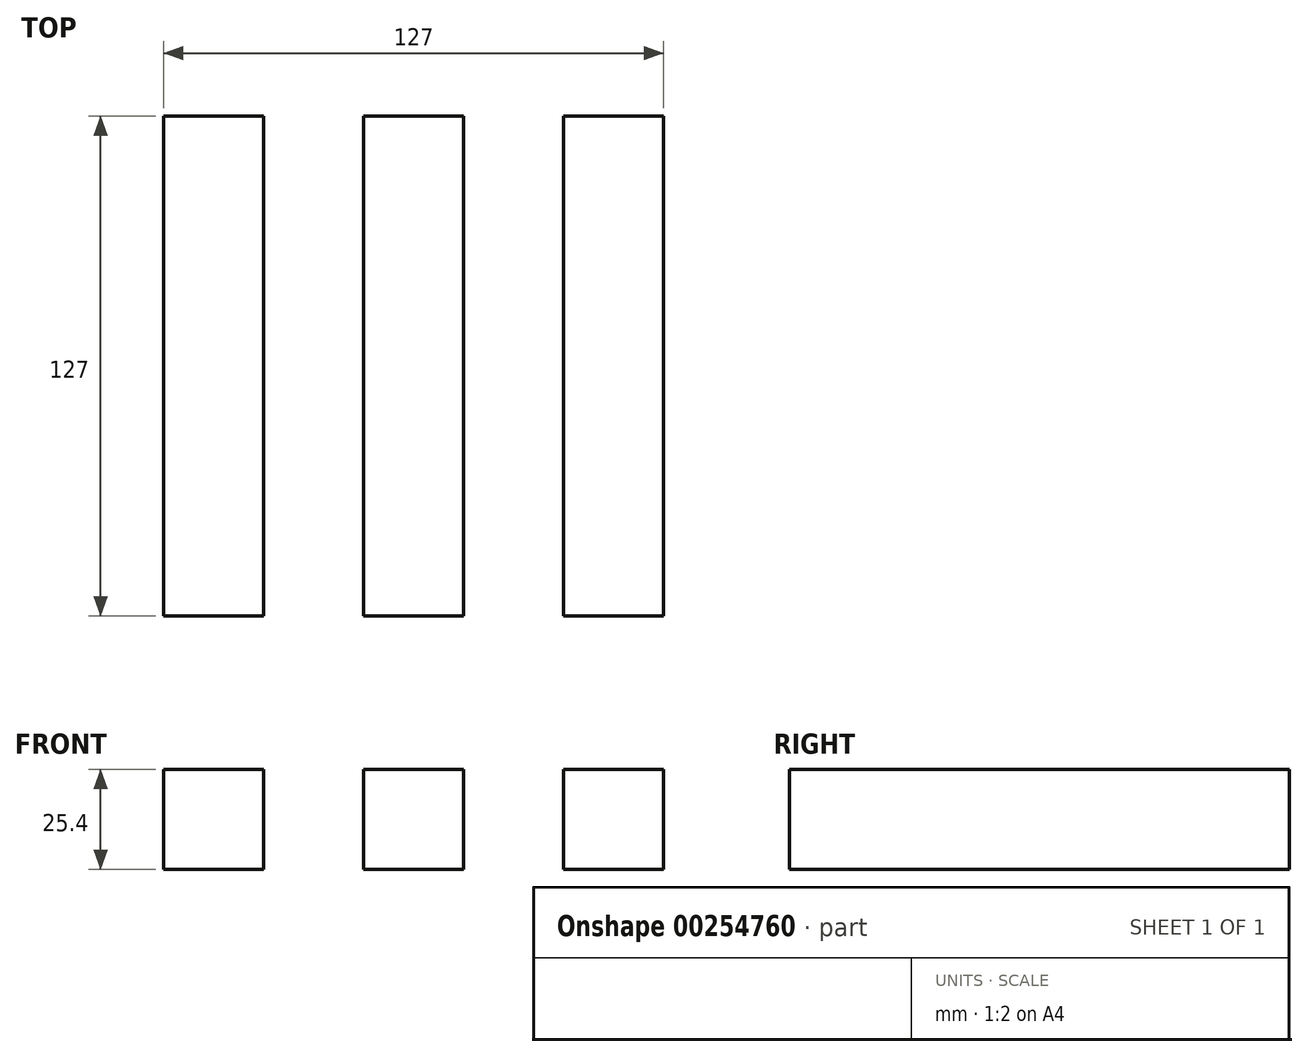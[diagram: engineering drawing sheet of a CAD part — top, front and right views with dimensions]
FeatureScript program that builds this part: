
annotation { "Feature Type Name" : "Feature", "Feature Type Description" : "" }
export const myFeature = defineFeature(function(context is Context, id is Id, definition is map)
    precondition{}
    {
        {
            var Q0;
            Q0=qCreatedBy(makeId("Front.planeOp"),FACE);
            var sketch = newSketch(context, id + "F0", { "sketchPlane" : qUnion([Q0])});
            skLineSegment(sketch, "E0.bottom", {"start": v(12.7, 12.7) * mm, "end": v(-12.7, 12.7) * mm});
            skLineSegment(sketch, "E0.top", {"start": v(12.7, -12.7) * mm, "end": v(-12.7, -12.7) * mm});
            skLineSegment(sketch, "E0.left", {"start": v(12.7, 12.7) * mm, "end": v(12.7, -12.7) * mm});
            skLineSegment(sketch, "E0.right", {"start": v(-12.7, 12.7) * mm, "end": v(-12.7, -12.7) * mm});
            skPoint(sketch, "E0.middle", {"position": v(0, 0) * mm});
            skLineSegment(sketch, "E1.bottom", {"start": v(63.5, 12.7) * mm, "end": v(38.1, 12.7) * mm});
            skLineSegment(sketch, "E1.top", {"start": v(63.5, -12.7) * mm, "end": v(38.1, -12.7) * mm});
            skLineSegment(sketch, "E1.left", {"start": v(63.5, 12.7) * mm, "end": v(63.5, -12.7) * mm});
            skLineSegment(sketch, "E1.right", {"start": v(38.1, 12.7) * mm, "end": v(38.1, -12.7) * mm});
            skPoint(sketch, "E1.middle", {"position": v(50.8, 0) * mm});
            skLineSegment(sketch, "E2.bottom", {"start": v(-38.1, 12.7) * mm, "end": v(-63.5, 12.7) * mm});
            skLineSegment(sketch, "E2.top", {"start": v(-38.1, -12.7) * mm, "end": v(-63.5, -12.7) * mm});
            skLineSegment(sketch, "E2.left", {"start": v(-38.1, 12.7) * mm, "end": v(-38.1, -12.7) * mm});
            skLineSegment(sketch, "E2.right", {"start": v(-63.5, 12.7) * mm, "end": v(-63.5, -12.7) * mm});
            skPoint(sketch, "E2.middle", {"position": v(-50.8, 0) * mm});
            skSolve(sketch);
        }
        {
            var Q0;
            Q0=makeQuery(id+"F0.imprint","IMPRINT",FACE,{"disambiguationData":[TD([[makeQuery(id+"F0.imprint","IMPRINT",EDGE,{"derivedFrom":sQuery(id+"F0.wireOp",EDGE,"E2.bottom")}),1.0]])]});
            var Q1;
            Q1=makeQuery(id+"F0.imprint","IMPRINT",FACE,{"disambiguationData":[TD([[makeQuery(id+"F0.imprint","IMPRINT",EDGE,{"derivedFrom":sQuery(id+"F0.wireOp",EDGE,"E0.bottom")}),1.0]])]});
            var Q2;
            Q2=makeQuery(id+"F0.imprint","IMPRINT",FACE,{"disambiguationData":[TD([[makeQuery(id+"F0.imprint","IMPRINT",EDGE,{"derivedFrom":sQuery(id+"F0.wireOp",EDGE,"E1.bottom")}),1.0]])]});
            extrude(context, id + "F1", {"entities" : qUnion([Q0, Q1, Q2]), "endBound" : BoundingType.SYMMETRIC, "depth" : 127 * mm});
        }
    });
